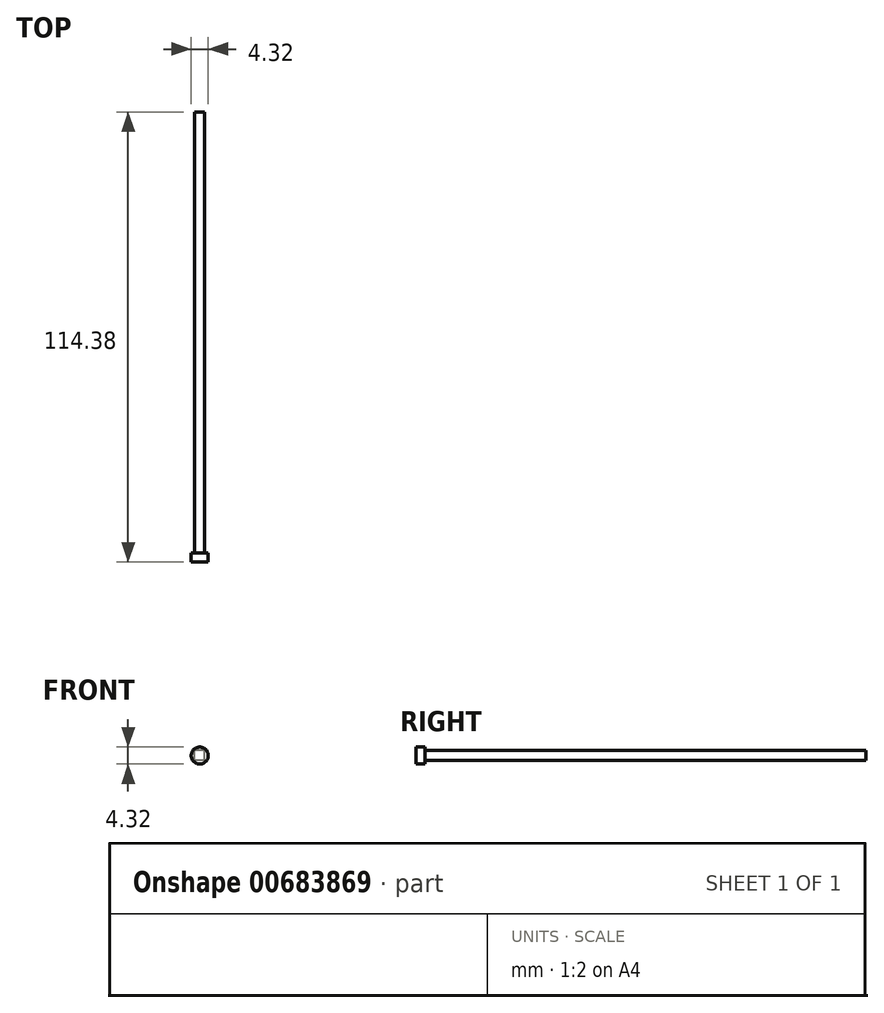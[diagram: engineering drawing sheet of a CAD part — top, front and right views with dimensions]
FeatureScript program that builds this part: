
annotation { "Feature Type Name" : "Feature", "Feature Type Description" : "" }
export const myFeature = defineFeature(function(context is Context, id is Id, definition is map)
    precondition{}
    {
        {
            var Q0;
            Q0=qCreatedBy(makeId("Front.planeOp"),FACE);
            var sketch = newSketch(context, id + "F0", { "sketchPlane" : qUnion([Q0])});
            skLineSegment(sketch, "E0.bottom", {"start": v(1.26, -1.26) * mm, "end": v(-1.26, -1.26) * mm});
            skLineSegment(sketch, "E0.top", {"start": v(1.26, 1.26) * mm, "end": v(-1.26, 1.26) * mm});
            skLineSegment(sketch, "E0.left", {"start": v(1.26, -1.26) * mm, "end": v(1.26, 1.26) * mm});
            skLineSegment(sketch, "E0.right", {"start": v(-1.26, -1.26) * mm, "end": v(-1.26, 1.26) * mm});
            skPoint(sketch, "E0.middle", {"position": v(0, 0) * mm});
            skSolve(sketch);
        }
        {
            var Q0;
            Q0 = qSketchRegion(id + "F0", true);
            extrude(context, id + "F1", {"entities" : qUnion([Q0]), "depth" : 56.05 * mm, "offsetDistance" : 25.4 * mm, "hasSecondDirection" : true, "secondDirectionOppositeDirection" : true, "secondDirectionDepth" : 56.05 * mm});
        }
        {
            var Q0;
            Q0=makeQuery(id+"F1.opExtrude","CAP_FACE",FACE,{"disambiguationData":[OSD([sQuery(id+"F0.wireOp",EDGE,"E0.bottom"),sQuery(id+"F0.wireOp",EDGE,"E0.top"),sQuery(id+"F0.wireOp",EDGE,"E0.left"),sQuery(id+"F0.wireOp",EDGE,"E0.right")])],"isStart":false});
            var sketch = newSketch(context, id + "F2", { "sketchPlane" : qUnion([Q0])});
            skCircle(sketch, "E1", {"center": v(0, 0) * mm, "radius": 2.16 * mm});
            skSolve(sketch);
        }
        {
            var Q0;
            Q0 = qSketchRegion(id + "F2", true);
            extrude(context, id + "F3", {"entities" : qUnion([Q0]), "operationType" : NewBodyOperationType.ADD, "depth" : 2.3 * mm, "offsetDistance" : 25.4 * mm});
        }
    });
